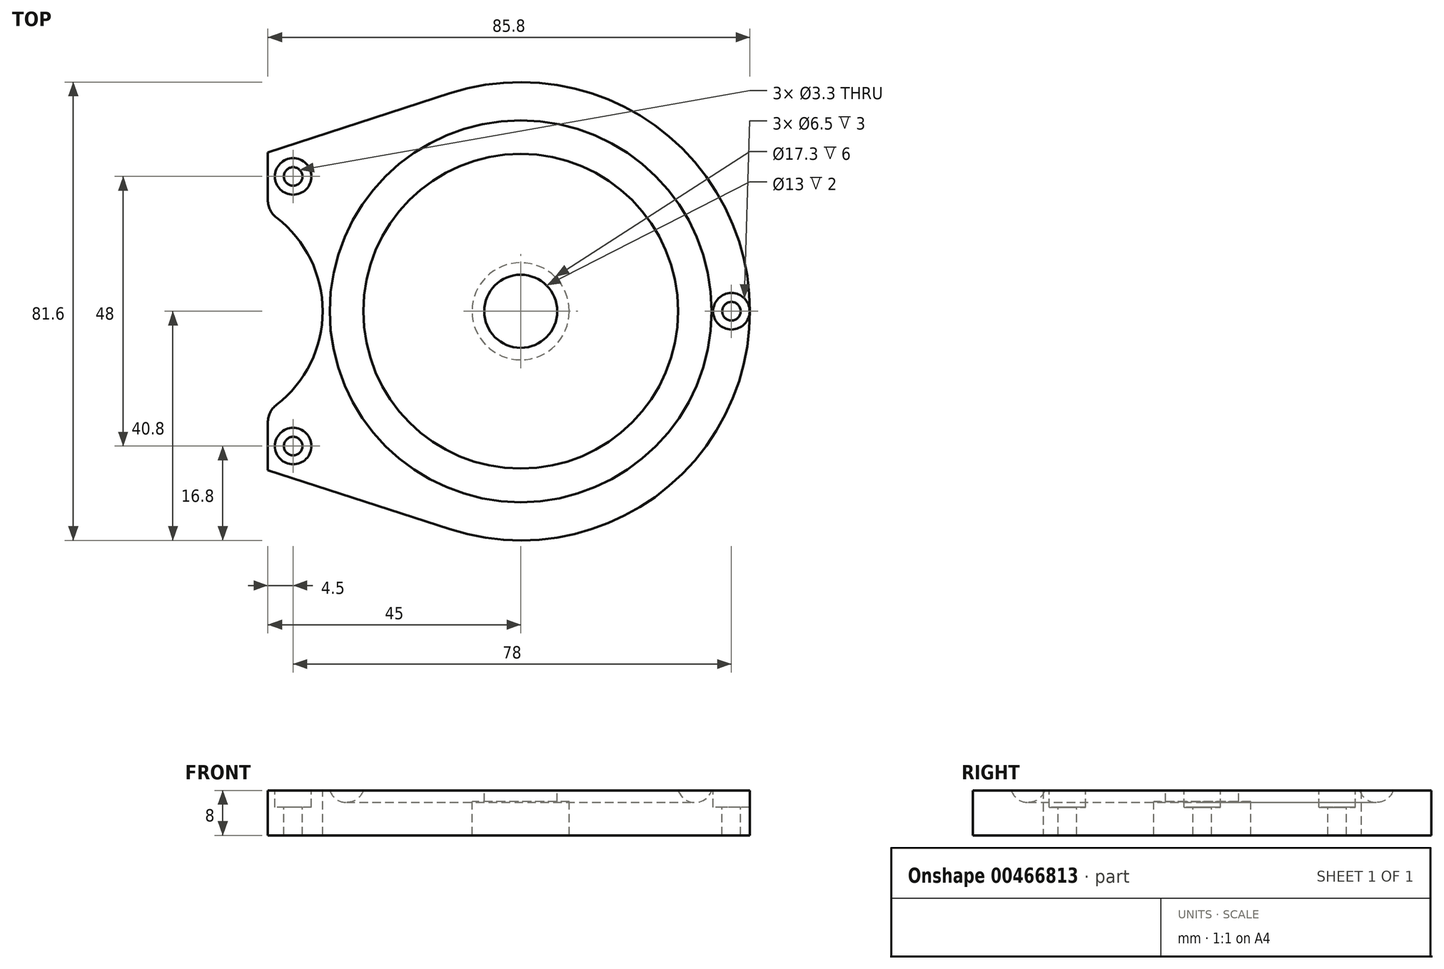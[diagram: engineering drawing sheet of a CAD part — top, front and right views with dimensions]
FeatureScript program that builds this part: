
annotation { "Feature Type Name" : "Feature", "Feature Type Description" : "" }
export const myFeature = defineFeature(function(context is Context, id is Id, definition is map)
    precondition{}
    {
        {
            var Q0;
            Q0=qCreatedBy(makeId("Top.planeOp"),FACE);
            var sketch = newSketch(context, id + "F0", { "sketchPlane" : qUnion([Q0])});
            skCircle(sketch, "E0", {"center": v(0, 0) * mm, "radius": 40.8 * mm});
            skSolve(sketch);
        }
        {
            var Q0;
            Q0=qSketchRegion(id+"F0",true);
            extrude(context, id + "F1", {"entities" : qUnion([Q0]), "depth" : 8 * mm, "offsetDistance" : 25 * mm});
        }
        {
            var Q0;
            Q0=qCreatedBy(makeId("Right.planeOp"),FACE);
            var sketch = newSketch(context, id + "F2", { "sketchPlane" : qUnion([Q0])});
            skLineSegment(sketch, "E1", {"start": v(0, 0) * mm, "end": v(0, 8) * mm});
            skLineSegment(sketch, "E2", {"start": v(0, 8) * mm, "end": v(6.5, 8) * mm});
            skLineSegment(sketch, "E3", {"start": v(6.5, 8) * mm, "end": v(6.5, 6) * mm});
            skLineSegment(sketch, "E4", {"start": v(6.5, 6) * mm, "end": v(8.65, 6) * mm});
            skLineSegment(sketch, "E5", {"start": v(8.65, 6) * mm, "end": v(8.65, 0) * mm});
            skLineSegment(sketch, "E6", {"start": v(8.65, 0) * mm, "end": v(0, 0) * mm});
            skLineSegment(sketch, "E7", {"start": v(0, 8) * mm, "end": v(0, 13.47) * mm, "construction": true});
            skSolve(sketch);
        }
        {
            var Q0;
            Q0=qSketchRegion(id+"F2",true);
            var Q1;
            Q1=sQuery(id+"F2.wireOp",EDGE,"E7");
            revolve(context, id + "F3", {"operationType" : NewBodyOperationType.REMOVE, "entities" : qUnion([Q0]), "axis" : qUnion([Q1]), "revolveType" : RevolveType.FULL, "oppositeDirection" : true});
        }
        {
            var Q0;
            Q0=qCreatedBy(makeId("Right.planeOp"),FACE);
            var sketch = newSketch(context, id + "F4", { "sketchPlane" : qUnion([Q0])});
            skCircle(sketch, "E8", {"center": v(31, 9) * mm, "radius": 3.15 * mm});
            skLineSegment(sketch, "E9", {"start": v(0, -0.8) * mm, "end": v(0, 13.57) * mm, "construction": true});
            skSolve(sketch);
        }
        {
            var Q0;
            Q0=qSketchRegion(id+"F4",true);
            var Q1;
            Q1=sQuery(id+"F4.wireOp",EDGE,"E9");
            revolve(context, id + "F5", {"operationType" : NewBodyOperationType.REMOVE, "entities" : qUnion([Q0]), "axis" : qUnion([Q1]), "revolveType" : RevolveType.FULL, "oppositeDirection" : true});
        }
        {
            var Q0;
            Q0=qCreatedBy(makeId("Top.planeOp"),FACE);
            var sketch = newSketch(context, id + "F6", { "sketchPlane" : qUnion([Q0])});
            skLineSegment(sketch, "E10.bottom", {"start": v(-36, 19.2) * mm, "end": v(-40.8, 19.2) * mm});
            skLineSegment(sketch, "E10.top", {"start": v(-36, -19.2) * mm, "end": v(-40.8, -19.2) * mm});
            skLineSegment(sketch, "E10.left", {"start": v(-36, 19.2) * mm, "end": v(-36, -19.2) * mm});
            skLineSegment(sketch, "E10.right", {"start": v(-40.8, 19.2) * mm, "end": v(-40.8, -19.2) * mm});
            skSolve(sketch);
        }
        {
            var Q0;
            Q0=qCreatedBy(makeId("Top.planeOp"),FACE);
            var sketch = newSketch(context, id + "F7", { "sketchPlane" : qUnion([Q0])});
            skLineSegment(sketch, "E11", {"start": v(-45, -28.28) * mm, "end": v(-45, 28.28) * mm});
            skLineSegment(sketch, "E12", {"start": v(-45, 28.28) * mm, "end": v(-12.6, 38.8) * mm});
            skLineSegment(sketch, "E13", {"start": v(0, 0) * mm, "end": v(-51.86, 0) * mm, "construction": true});
            skArc(sketch, "E14.0", {"start": v(-12.6, 38.8) * mm, "mid": v(-26.2, 31.27) * mm, "end": v(-36, 19.2) * mm});
            skPoint(sketch, "E15.orphan", {"position": v(-36, -19.2) * mm});
            skLineSegment(sketch, "E16.MirrorCS", {"start": v(-45, -28.28) * mm, "end": v(-12.6, -38.8) * mm});
            skArc(sketch, "E17.MirrorCS", {"start": v(-12.6, -38.8) * mm, "mid": v(-26.2, -31.27) * mm, "end": v(-36, -19.2) * mm});
            skLineSegment(sketch, "E18", {"start": v(-36, 19.2) * mm, "end": v(-36, -19.2) * mm});
            skSolve(sketch);
        }
        {
            var Q0;
            Q0=qSketchRegion(id+"F7",true);
            var Q1;
            {var subQ0=sQuery(id+"F0.wireOp",EDGE,"E0");Q1=makeQuery(id+"F5.boolean.opBoolean","SPLIT",FACE,{"disambiguationData":[TD([makeQuery(id+"F1.opExtrude","SWEPT_FACE",FACE,{"disambiguationData":[OSD([subQ0])]})])],"derivedFrom":makeQuery(id+"F1.opExtrude","CAP_FACE",FACE,{"disambiguationData":[OSD([subQ0])],"isStart":false})});}
            extrude(context, id + "F8", {"entities" : qUnion([Q0]), "operationType" : NewBodyOperationType.ADD, "endBound" : BoundingType.UP_TO_SURFACE, "endBoundEntityFace" : qUnion([Q1]), "depth" : 25 * mm, "offsetDistance" : 25 * mm});
        }
        {
            var Q0;
            {var subQ0=sQuery(id+"F0.wireOp",EDGE,"E0");Q0=makeQuery(id+"F8.boolean.opBoolean","MERGE",FACE,{"derivedFrom":[makeQuery(id+"F5.boolean.opBoolean","SPLIT",FACE,{"disambiguationData":[TD([makeQuery(id+"F1.opExtrude","SWEPT_FACE",FACE,{"disambiguationData":[OSD([subQ0])]})])],"derivedFrom":makeQuery(id+"F1.opExtrude","CAP_FACE",FACE,{"disambiguationData":[OSD([subQ0])],"isStart":false})}),makeQuery(id+"F8.opExtrude","CAP_FACE",FACE,{"disambiguationData":[OSD([sQuery(id+"F7.wireOp",EDGE,"E11"),sQuery(id+"F7.wireOp",EDGE,"E12"),sQuery(id+"F7.wireOp",EDGE,"E14.0"),sQuery(id+"F7.wireOp",EDGE,"E16.MirrorCS"),sQuery(id+"F7.wireOp",EDGE,"E17.MirrorCS"),sQuery(id+"F7.wireOp",EDGE,"E18")])],"isStart":false})]});}
            var sketch = newSketch(context, id + "F9", { "sketchPlane" : qUnion([Q0])});
            skCircle(sketch, "E19", {"center": v(-56.25, 0) * mm, "radius": 21 * mm});
            skLineSegment(sketch, "E20", {"start": v(-56.25, 0) * mm, "end": v(0, 0) * mm, "construction": true});
            skSolve(sketch);
        }
        {
            var Q0;
            Q0=qSketchRegion(id+"F9",true);
            extrude(context, id + "F10", {"entities" : qUnion([Q0]), "operationType" : NewBodyOperationType.REMOVE, "endBound" : BoundingType.THROUGH_ALL, "oppositeDirection" : true, "depth" : 25 * mm, "offsetDistance" : 25 * mm});
        }
        {
            var Q0;
            Q0=makeQuery(id+"F10.boolean.opBoolean","INTERSECT",EDGE,{"disambiguationData":[OD(1.0)],"derivedFrom":[makeQuery(id+"F8.opExtrude","SWEPT_FACE",FACE,{"disambiguationData":[OSD([sQuery(id+"F7.wireOp",EDGE,"E11")])]}),makeQuery(id+"F10.opExtrude","SWEPT_FACE",FACE,{"disambiguationData":[OSD([sQuery(id+"F9.wireOp",EDGE,"E19")])]})]});
            var Q1;
            Q1=makeQuery(id+"F10.boolean.opBoolean","INTERSECT",EDGE,{"disambiguationData":[OD(0.0)],"derivedFrom":[makeQuery(id+"F8.opExtrude","SWEPT_FACE",FACE,{"disambiguationData":[OSD([sQuery(id+"F7.wireOp",EDGE,"E11")])]}),makeQuery(id+"F10.opExtrude","SWEPT_FACE",FACE,{"disambiguationData":[OSD([sQuery(id+"F9.wireOp",EDGE,"E19")])]})]});
            fillet(context, id + "F11", {"entities" : qUnion([Q0, Q1]), "radius" : 4 * mm, "tangentPropagation" : true, "allowEdgeOverflow" : false});
        }
        {
            var Q0;
            {var subQ0=sQuery(id+"F0.wireOp",EDGE,"E0");Q0=makeQuery(id+"F8.boolean.opBoolean","MERGE",FACE,{"derivedFrom":[makeQuery(id+"F5.boolean.opBoolean","SPLIT",FACE,{"disambiguationData":[TD([makeQuery(id+"F1.opExtrude","SWEPT_FACE",FACE,{"disambiguationData":[OSD([subQ0])]})])],"derivedFrom":makeQuery(id+"F1.opExtrude","CAP_FACE",FACE,{"disambiguationData":[OSD([subQ0])],"isStart":false})}),makeQuery(id+"F8.opExtrude","CAP_FACE",FACE,{"disambiguationData":[OSD([sQuery(id+"F7.wireOp",EDGE,"E11"),sQuery(id+"F7.wireOp",EDGE,"E12"),sQuery(id+"F7.wireOp",EDGE,"E14.0"),sQuery(id+"F7.wireOp",EDGE,"E16.MirrorCS"),sQuery(id+"F7.wireOp",EDGE,"E17.MirrorCS"),sQuery(id+"F7.wireOp",EDGE,"E18")])],"isStart":false})]});}
            var sketch = newSketch(context, id + "F12", { "sketchPlane" : qUnion([Q0])});
            skPoint(sketch, "E21", {"position": v(-40.5, 24) * mm});
            skPoint(sketch, "E22", {"position": v(37.5, 0) * mm});
            skLineSegment(sketch, "E23", {"start": v(0, 0) * mm, "end": v(47.97, 0) * mm, "construction": true});
            skPoint(sketch, "E24.MirrorP", {"position": v(-40.5, -24) * mm});
            skSolve(sketch);
        }
        {
            var Q0;
            Q0=sQuery(id+"F12.wireOp",VERTEX,"E21");
            var Q1;
            Q1=sQuery(id+"F12.wireOp",VERTEX,"E24.MirrorP");
            var Q2;
            Q2=sQuery(id+"F12.wireOp",VERTEX,"E22");
            var Q3;
            Q3=makeQuery(id+"F1.opExtrude","SWEPT_BODY",BODY,{"disambiguationData":[OSD([sQuery(id+"F0.wireOp",EDGE,"E0")])]});
            hole(context, id + "F13", {"style" : HoleStyle.C_BORE, "endStyle" : HoleEndStyle.THROUGH, "standardTappedOrClearance" : lookupTablePath({ "standard" : "ISO", "fit" : "Normal", "size" : "M3", "type" : "Clearance" }), "standardBlindInLast" : lookupTablePath({ "fit" : "Standard", "standard" : "ISO", "size" : "M3", "type" : "Clearance" }), "holeDiameter" : 3.3 * mm, "cBoreDiameter" : 6.5 * mm, "cBoreDepth" : 3 * mm, "tappedDepth" : 12 * mm, "tapClearance" : 3, "locations" : qUnion([Q0, Q1, Q2]), "scope" : qUnion([Q3])});
        }
    });
